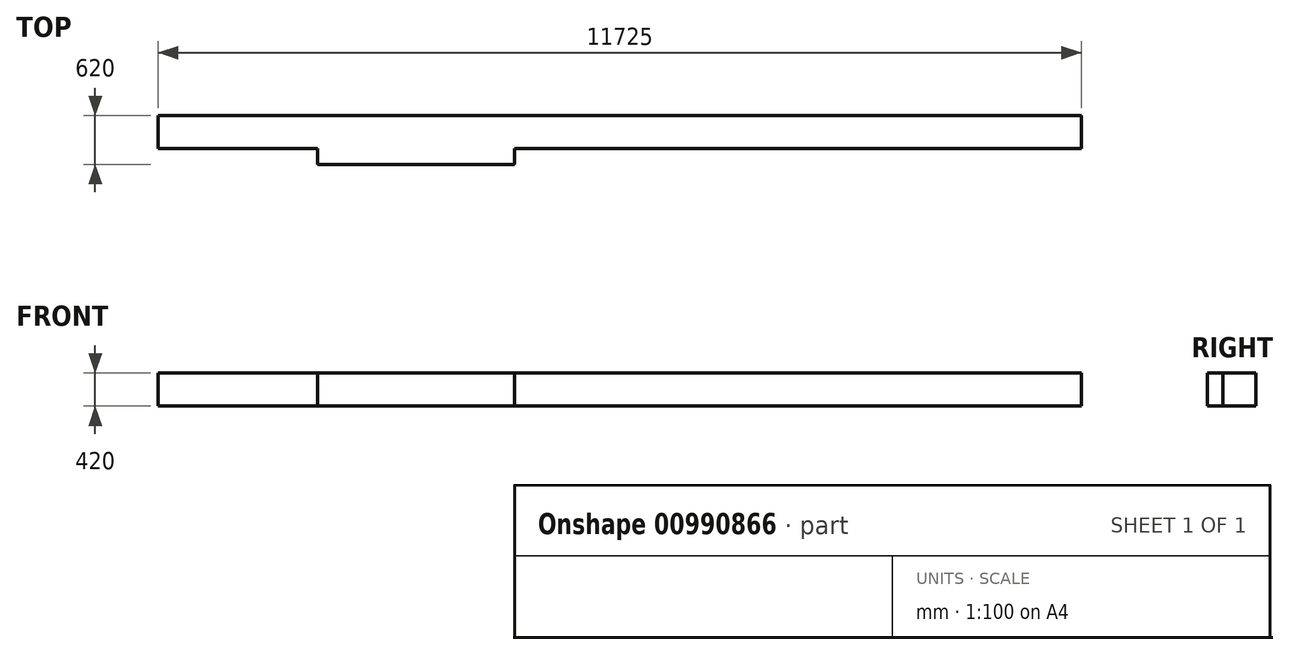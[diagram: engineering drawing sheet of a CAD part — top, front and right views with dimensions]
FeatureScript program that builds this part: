
annotation { "Feature Type Name" : "Feature", "Feature Type Description" : "" }
export const myFeature = defineFeature(function(context is Context, id is Id, definition is map)
    precondition{}
    {
        {
            var Q0;
            Q0=qCreatedBy(makeId("Top.planeOp"),FACE);
            var sketch = newSketch(context, id + "F0", { "sketchPlane" : qUnion([Q0])});
            skLineSegment(sketch, "E0", {"start": v(-62.87, 342.83) * mm, "end": v(-62.87, -77.17) * mm});
            skLineSegment(sketch, "E1", {"start": v(-62.87, 342.83) * mm, "end": v(4212.13, 342.83) * mm});
            skLineSegment(sketch, "E2", {"start": v(11662.13, -77.17) * mm, "end": v(11662.13, 342.83) * mm});
            skLineSegment(sketch, "E3", {"start": v(11662.13, 342.83) * mm, "end": v(4212.13, 342.83) * mm});
            skLineSegment(sketch, "E4", {"start": v(3162.13, -77.17) * mm, "end": v(3162.13, -277.17) * mm});
            skLineSegment(sketch, "E5", {"start": v(3162.13, -277.17) * mm, "end": v(4162.13, -277.17) * mm});
            skLineSegment(sketch, "E6", {"start": v(5662.13, -77.17) * mm, "end": v(11662.13, -77.17) * mm});
            skPoint(sketch, "E7.start.orphan", {"position": v(3162.13, -1211.23) * mm});
            skLineSegment(sketch, "E8.0", {"start": v(4462.13, -277.17) * mm, "end": v(4462.13, -77.17) * mm});
            skLineSegment(sketch, "E9.0", {"start": v(1962.13, -277.17) * mm, "end": v(1962.13, -77.17) * mm});
            skLineSegment(sketch, "E10", {"start": v(4462.13, -277.17) * mm, "end": v(1962.13, -277.17) * mm});
            skLineSegment(sketch, "E11", {"start": v(5662.13, -77.17) * mm, "end": v(4462.13, -77.17) * mm});
            skLineSegment(sketch, "E12", {"start": v(-62.87, -77.17) * mm, "end": v(1962.13, -77.17) * mm});
            skSolve(sketch);
        }
        {
            var Q0;
            Q0=makeQuery(id+"F0.imprint","IMPRINT",FACE,{"disambiguationData":[TD([[makeQuery(id+"F0.imprint","IMPRINT",EDGE,{"derivedFrom":sQuery(id+"F0.wireOp",EDGE,"E0")}),1.0]])]});
            extrude(context, id + "F1", {"entities" : qUnion([Q0]), "depth" : 420 * mm, "offsetDistance" : 25 * mm});
        }
    });
